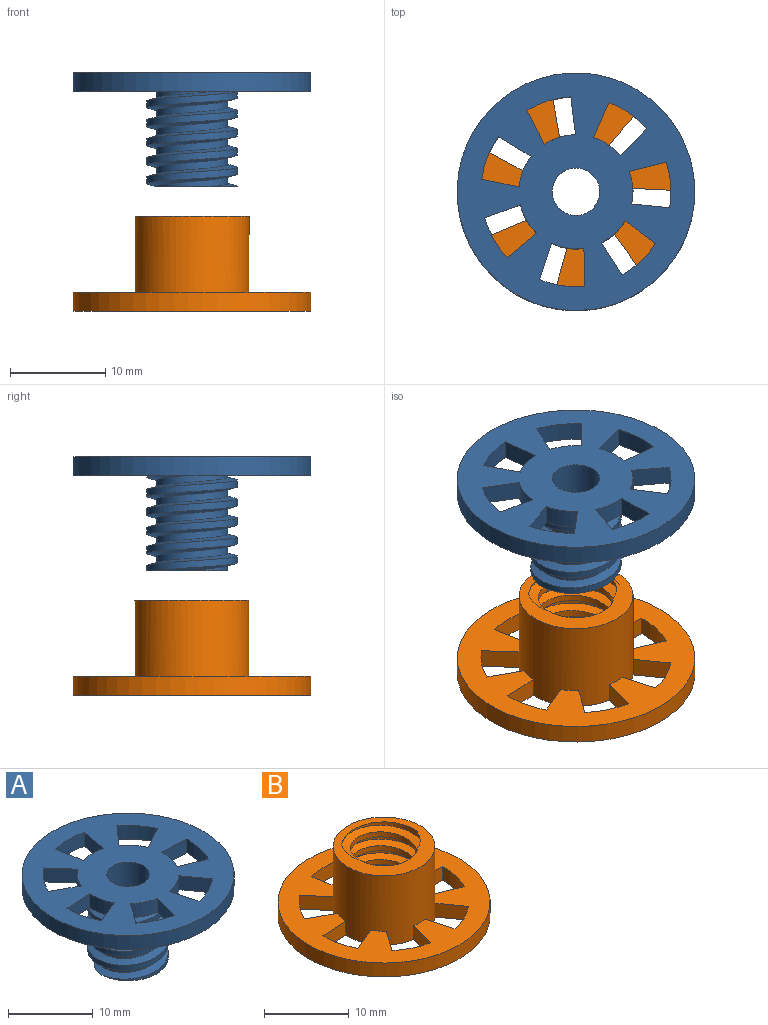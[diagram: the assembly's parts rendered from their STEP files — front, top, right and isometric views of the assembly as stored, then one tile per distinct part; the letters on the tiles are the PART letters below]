
ASSEMBLY  parts=2 mates=1
PART A: 37 faces, bbox 25x25x12.3 mm
  f0: cylinder r=6mm len=3.35mm, axis (0,0,-1), area 7mm2, adj f1,f21,f29,f30
  f1: plane 4.01x2mm, normal (-0.05,-1,0), area 8mm2, adj f0,f2,f29,f30
  f2: cylinder r=10mm len=4.71mm, axis (0,0,-1), area 9.8mm2, adj f1,f21,f29,f30
  f3: plane 3.87x2mm, normal (0.96,0.27,0), area 8mm2, adj f4,f22,f29,f30
  f4: cylinder r=6mm len=3.09mm, axis (0,0,-1), area 7mm2, adj f3,f5,f29,f30
  f5: plane 3.26x2.34mm, normal (-0.81,-0.58,0), area 8mm2, adj f4,f22,f29,f30
  f6: plane 3.26x2.34mm, normal (0.81,-0.58,0), area 8mm2, adj f7,f23,f29,f30
  f7: cylinder r=6mm len=3.09mm, axis (0,0,-1), area 7mm2, adj f6,f8,f29,f30
  f8: plane 3.87x2mm, normal (-0.96,0.27,0), area 8mm2, adj f7,f23,f29,f30
  f9: plane 4.01x2mm, normal (0.05,-1,0), area 8mm2, adj f10,f24,f29,f30
  f10: cylinder r=6mm len=3.35mm, axis (0,0,-1), area 7mm2, adj f9,f11,f29,f30
  f11: plane 3.7x2mm, normal (-0.39,0.92,0), area 8mm2, adj f10,f24,f29,f30
  f12: plane 3.01x2.66mm, normal (-0.75,-0.66,0), area 8mm2, adj f13,f25,f29,f30
  f13: cylinder r=6mm len=2.68mm, axis (0,0,-1), area 7mm2, adj f12,f14,f29,f30
  f14: plane 3.53x2mm, normal (0.48,0.88,0), area 8mm2, adj f13,f25,f29,f30
  f15: plane 3.96x2mm, normal (-0.98,0.17,0), area 8mm2, adj f16,f26,f29,f30
  f16: cylinder r=6mm len=3.43mm, axis (0,0,-1), area 7mm2, adj f15,f17,f29,f30
  f17: plane 3.96x2mm, normal (0.98,0.17,0), area 8mm2, adj f16,f26,f29,f30
  f18: plane 3.53x2mm, normal (-0.48,0.88,0), area 8mm2, adj f19,f27,f29,f30
  f19: cylinder r=6mm len=2.68mm, axis (0,0,-1), area 7mm2, adj f18,f20,f29,f30
  f20: plane 3.01x2.66mm, normal (0.75,-0.66,0), area 8mm2, adj f19,f27,f29,f30
  f21: plane 3.7x2mm, normal (0.39,0.92,0), area 8mm2, adj f0,f2,f29,f30
  f22: cylinder r=10mm len=4.35mm, axis (0,0,-1), area 9.8mm2, adj f3,f5,f29,f30
  f23: cylinder r=10mm len=4.35mm, axis (0,0,-1), area 9.8mm2, adj f6,f8,f29,f30
  f24: cylinder r=10mm len=4.71mm, axis (0,0,-1), area 9.8mm2, adj f9,f11,f29,f30
  f25: cylinder r=10mm len=3.77mm, axis (0,0,-1), area 9.8mm2, adj f12,f14,f29,f30
  f26: cylinder r=10mm len=4.83mm, axis (0,0,-1), area 9.8mm2, adj f15,f17,f29,f30
  f27: cylinder r=10mm len=3.77mm, axis (0,0,-1), area 9.8mm2, adj f18,f20,f29,f30
  f28: cylinder r=12.5mm len=25mm, axis (0,0,-1), area 157.1mm2, adj f29,f30
  f29: plane 25x25mm, normal (0,0,1), area 354.2mm2, adj f0,f1,f2,f3,f4,f5,f6,f7
  f30: plane 25x25mm, normal (0,0,-1), area 316.6mm2, adj f0,f1,f2,f3,f4,f5,f6,f7
  f31: cylinder r=4.75mm len=10mm, axis (0,0,-1), area 108.5mm2, adj f30,f32,f35,f36
  f32: plane 8.63x8.5mm, normal (0,0,-1), area 37.6mm2, adj f31,f33,f34,f35,f36
  f33: cylinder r=2.5mm len=12mm, axis (0,0,-1), area 188.5mm2, adj f29,f32
  f34: cylinder r=3.75mm len=10mm, axis (0,0,1), area 87.4mm2, adj f30,f32,f35,f36
  f35: bspline ~10.97x10.6mm, area 138.6mm2, adj f30,f31,f32,f34
  f36: bspline ~10.97x10.6mm, area 138.6mm2, adj f30,f31,f32,f34
PART B: 30 faces, bbox 25x25x10.6 mm
  f0: cylinder r=5mm len=10mm, axis (0,0,-1), area 117.5mm2, adj f25,f26,f28,f29
  f1: plane 25x25mm, normal (0,0,1), area 260.8mm2, adj f2,f3,f4,f5,f6,f7,f8,f9
  f2: cylinder r=10mm len=4.35mm, axis (0,0,-1), area 9.8mm2, adj f1,f3,f17,f25
  f3: plane 3.87x2mm, normal (0.96,0.27,0), area 8mm2, adj f1,f2,f23,f25
  f4: cylinder r=10mm len=4.35mm, axis (0,0,-1), area 9.8mm2, adj f1,f5,f18,f25
  f5: plane 3.26x2.34mm, normal (0.81,-0.58,0), area 8mm2, adj f1,f4,f23,f25
  f6: cylinder r=10mm len=4.71mm, axis (0,0,-1), area 9.8mm2, adj f1,f7,f19,f25
  f7: plane 4.01x2mm, normal (0.05,-1,0), area 8mm2, adj f1,f6,f23,f25
  f8: cylinder r=10mm len=3.77mm, axis (0,0,-1), area 9.8mm2, adj f1,f9,f20,f25
  f9: plane 3.01x2.66mm, normal (-0.75,-0.66,0), area 8mm2, adj f1,f8,f23,f25
  f10: cylinder r=10mm len=4.83mm, axis (0,0,-1), area 9.8mm2, adj f1,f11,f21,f25
  f11: plane 3.96x2mm, normal (-0.98,0.17,0), area 8mm2, adj f1,f10,f23,f25
  f12: cylinder r=10mm len=3.77mm, axis (0,0,-1), area 9.8mm2, adj f1,f13,f22,f25
  f13: plane 3.53x2mm, normal (-0.48,0.88,0), area 8mm2, adj f1,f12,f23,f25
  f14: plane 4.01x2mm, normal (-0.05,-1,0), area 8mm2, adj f1,f15,f23,f25
  f15: cylinder r=10mm len=4.71mm, axis (0,0,-1), area 9.8mm2, adj f1,f14,f16,f25
  f16: plane 3.7x2mm, normal (0.39,0.92,0), area 8mm2, adj f1,f15,f23,f25
  f17: plane 3.26x2.34mm, normal (-0.81,-0.58,0), area 8mm2, adj f1,f2,f23,f25
  f18: plane 3.87x2mm, normal (-0.96,0.27,0), area 8mm2, adj f1,f4,f23,f25
  f19: plane 3.7x2mm, normal (-0.39,0.92,0), area 8mm2, adj f1,f6,f23,f25
  f20: plane 3.53x2mm, normal (0.48,0.88,0), area 8mm2, adj f1,f8,f23,f25
  f21: plane 3.96x2mm, normal (0.98,0.17,0), area 8mm2, adj f1,f10,f23,f25
  f22: plane 3.01x2.66mm, normal (0.75,-0.66,0), area 8mm2, adj f1,f12,f23,f25
  f23: cylinder r=6mm len=12mm, axis (0,0,-1), area 350.3mm2, adj f1,f3,f5,f7,f9,f11,f13,f14
  f24: cylinder r=12.5mm len=25mm, axis (0,0,-1), area 157.1mm2, adj f1,f25
  f25: plane 25x25mm, normal (0,0,-1), area 309.5mm2, adj f0,f2,f3,f4,f5,f6,f7,f8
  f26: plane 12x12mm, normal (0,0,1), area 48.7mm2, adj f0,f23,f27,f28,f29
  f27: cylinder r=4mm len=10mm, axis (0,0,1), area 91.1mm2, adj f25,f26,f28,f29
  f28: bspline ~11.55x10.6mm, area 146.6mm2, adj f0,f25,f26,f27
  f29: bspline ~11.55x10.6mm, area 146.6mm2, adj f0,f25,f26,f27
PLACE A rot(axis=(0,0,1),171.4deg) t=(0,0,27.3)mm
PLACE B t=(0,0,14.2)mm fixed
MATE cylindrical B.f0 <-> A.f0  axis (0,0,-1) through (0,0,14.2)mm
